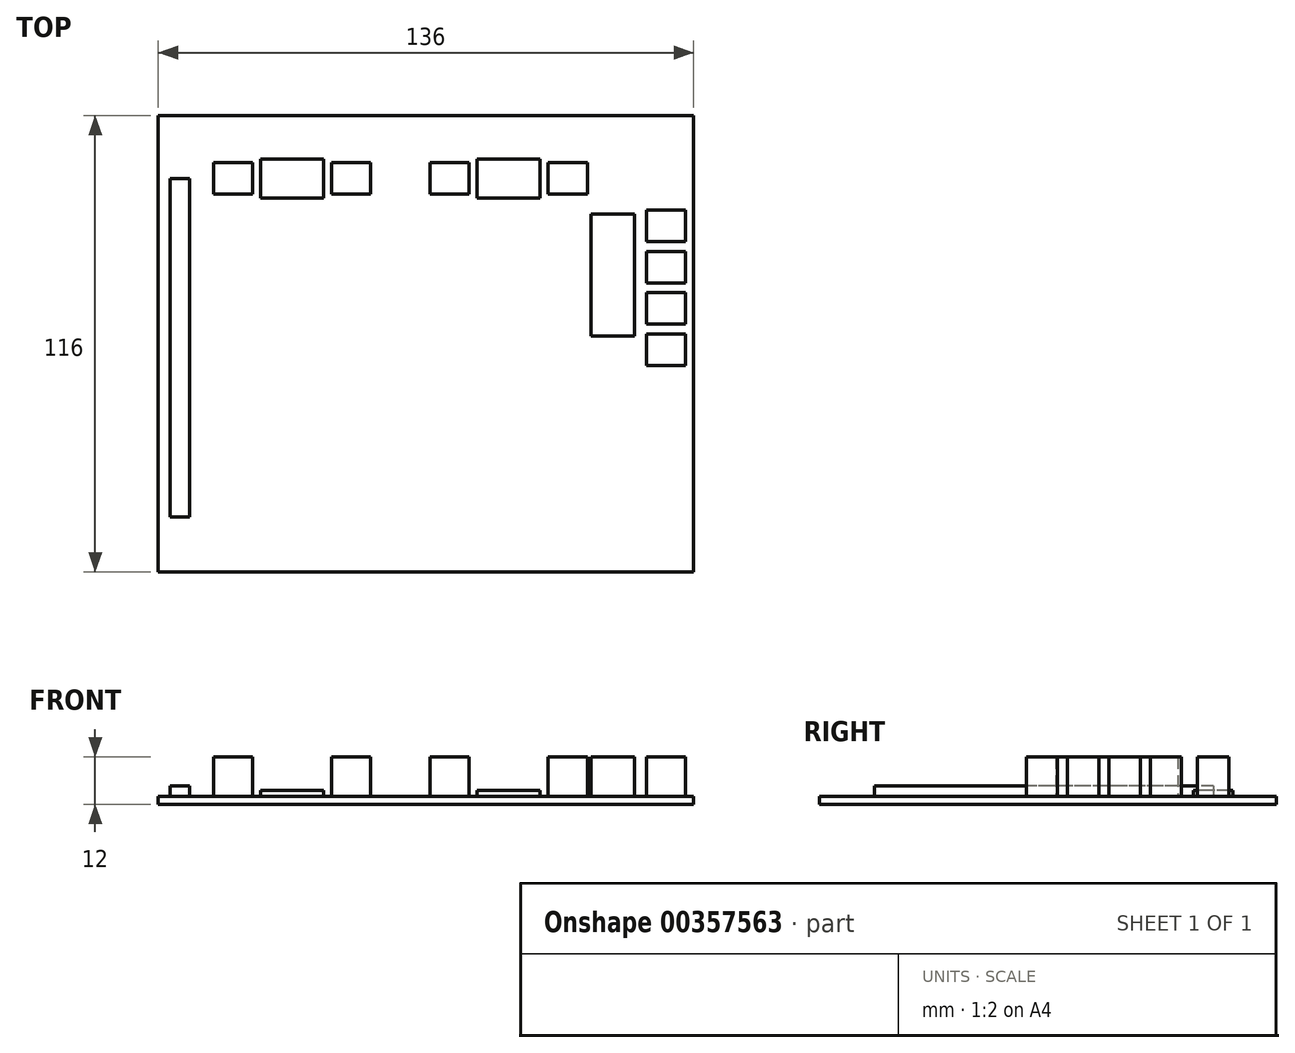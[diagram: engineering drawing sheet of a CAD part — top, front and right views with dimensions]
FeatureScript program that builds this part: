
annotation { "Feature Type Name" : "Feature", "Feature Type Description" : "" }
export const myFeature = defineFeature(function(context is Context, id is Id, definition is map)
    precondition{}
    {
        {
            var Q0;
            Q0=qCreatedBy(makeId("Top.planeOp"),FACE);
            var sketch = newSketch(context, id + "F0", { "sketchPlane" : qUnion([Q0])});
            skLineSegment(sketch, "E0.bottom", {"start": v(-68, -58) * mm, "end": v(68, -58) * mm});
            skLineSegment(sketch, "E0.top", {"start": v(-68, 58) * mm, "end": v(68, 58) * mm});
            skLineSegment(sketch, "E0.left", {"start": v(-68, -58) * mm, "end": v(-68, 58) * mm});
            skLineSegment(sketch, "E0.right", {"start": v(68, -58) * mm, "end": v(68, 58) * mm});
            skPoint(sketch, "E0.middle", {"position": v(0, 0) * mm});
            skSolve(sketch);
        }
        {
            var Q0;
            Q0=makeQuery(id+"F0.imprint","IMPRINT",FACE,{"disambiguationData":[TD([[makeQuery(id+"F0.imprint","IMPRINT",EDGE,{"derivedFrom":sQuery(id+"F0.wireOp",EDGE,"E0.bottom")}),1.0]])]});
            extrude(context, id + "F1", {"entities" : qUnion([Q0]), "endBound" : BoundingType.SYMMETRIC, "depth" : 2 * mm});
        }
        {
            var Q0;
            Q0=makeQuery(id+"F1.opExtrude","CAP_FACE",FACE,{"disambiguationData":[OSD([sQuery(id+"F0.wireOp",EDGE,"E0.bottom"),sQuery(id+"F0.wireOp",EDGE,"E0.top"),sQuery(id+"F0.wireOp",EDGE,"E0.left"),sQuery(id+"F0.wireOp",EDGE,"E0.right")])],"isStart":false});
            var sketch = newSketch(context, id + "F2", { "sketchPlane" : qUnion([Q0])});
            skLineSegment(sketch, "E1.bottom", {"start": v(53, 2) * mm, "end": v(42, 2) * mm});
            skLineSegment(sketch, "E1.top", {"start": v(53, 33) * mm, "end": v(42, 33) * mm});
            skLineSegment(sketch, "E1.left", {"start": v(53, 2) * mm, "end": v(53, 33) * mm});
            skLineSegment(sketch, "E1.right", {"start": v(42, 2) * mm, "end": v(42, 33) * mm});
            skPoint(sketch, "E1.middle", {"position": v(47.5, 17.5) * mm});
            skLineSegment(sketch, "E2.bottom", {"start": v(29, 37) * mm, "end": v(13, 37) * mm});
            skLineSegment(sketch, "E2.top", {"start": v(29, 47) * mm, "end": v(13, 47) * mm});
            skLineSegment(sketch, "E2.left", {"start": v(29, 47) * mm, "end": v(29, 37) * mm});
            skLineSegment(sketch, "E2.right", {"start": v(13, 47) * mm, "end": v(13, 37) * mm});
            skLineSegment(sketch, "E3.bottom", {"start": v(-26, 37) * mm, "end": v(-42, 37) * mm});
            skLineSegment(sketch, "E3.top", {"start": v(-26, 47) * mm, "end": v(-42, 47) * mm});
            skLineSegment(sketch, "E3.left", {"start": v(-26, 47) * mm, "end": v(-26, 37) * mm});
            skLineSegment(sketch, "E3.right", {"start": v(-42, 47) * mm, "end": v(-42, 37) * mm});
            skLineSegment(sketch, "E4.bottom", {"start": v(-65, 42) * mm, "end": v(-60, 42) * mm});
            skLineSegment(sketch, "E4.top", {"start": v(-65, -44) * mm, "end": v(-60, -44) * mm});
            skLineSegment(sketch, "E4.left", {"start": v(-65, 42) * mm, "end": v(-65, -44) * mm});
            skLineSegment(sketch, "E4.right", {"start": v(-60, 42) * mm, "end": v(-60, -44) * mm});
            skLineSegment(sketch, "E5.bottom", {"start": v(-54, 46) * mm, "end": v(-44, 46) * mm});
            skLineSegment(sketch, "E5.top", {"start": v(-54, 38) * mm, "end": v(-44, 38) * mm});
            skLineSegment(sketch, "E5.left", {"start": v(-54, 46) * mm, "end": v(-54, 38) * mm});
            skLineSegment(sketch, "E5.right", {"start": v(-44, 46) * mm, "end": v(-44, 38) * mm});
            skLineSegment(sketch, "E6.bottom", {"start": v(-24, 46) * mm, "end": v(-14, 46) * mm});
            skLineSegment(sketch, "E6.top", {"start": v(-24, 38) * mm, "end": v(-14, 38) * mm});
            skLineSegment(sketch, "E6.left", {"start": v(-24, 46) * mm, "end": v(-24, 38) * mm});
            skLineSegment(sketch, "E6.right", {"start": v(-14, 46) * mm, "end": v(-14, 38) * mm});
            skLineSegment(sketch, "E7.bottom", {"start": v(1, 46) * mm, "end": v(11, 46) * mm});
            skLineSegment(sketch, "E7.top", {"start": v(1, 38) * mm, "end": v(11, 38) * mm});
            skLineSegment(sketch, "E7.left", {"start": v(1, 46) * mm, "end": v(1, 38) * mm});
            skLineSegment(sketch, "E7.right", {"start": v(11, 46) * mm, "end": v(11, 38) * mm});
            skLineSegment(sketch, "E8.bottom", {"start": v(31, 46) * mm, "end": v(41, 46) * mm});
            skLineSegment(sketch, "E8.top", {"start": v(31, 38) * mm, "end": v(41, 38) * mm});
            skLineSegment(sketch, "E8.left", {"start": v(31, 46) * mm, "end": v(31, 38) * mm});
            skLineSegment(sketch, "E8.right", {"start": v(41, 46) * mm, "end": v(41, 38) * mm});
            skLineSegment(sketch, "E9.bottom", {"start": v(56, 34) * mm, "end": v(66, 34) * mm});
            skLineSegment(sketch, "E9.top", {"start": v(56, 26) * mm, "end": v(66, 26) * mm});
            skLineSegment(sketch, "E9.left", {"start": v(56, 34) * mm, "end": v(56, 26) * mm});
            skLineSegment(sketch, "E9.right", {"start": v(66, 34) * mm, "end": v(66, 26) * mm});
            skLineSegment(sketch, "E10.bottom", {"start": v(56, 23.5) * mm, "end": v(66, 23.5) * mm});
            skLineSegment(sketch, "E10.top", {"start": v(56, 15.5) * mm, "end": v(66, 15.5) * mm});
            skLineSegment(sketch, "E10.left", {"start": v(56, 23.5) * mm, "end": v(56, 15.5) * mm});
            skLineSegment(sketch, "E10.right", {"start": v(66, 23.5) * mm, "end": v(66, 15.5) * mm});
            skLineSegment(sketch, "E11.bottom", {"start": v(56, 13) * mm, "end": v(66, 13) * mm});
            skLineSegment(sketch, "E11.top", {"start": v(56, 5) * mm, "end": v(66, 5) * mm});
            skLineSegment(sketch, "E11.left", {"start": v(56, 13) * mm, "end": v(56, 5) * mm});
            skLineSegment(sketch, "E11.right", {"start": v(66, 13) * mm, "end": v(66, 5) * mm});
            skLineSegment(sketch, "E12.bottom", {"start": v(56, 2.5) * mm, "end": v(66, 2.5) * mm});
            skLineSegment(sketch, "E12.top", {"start": v(56, -5.5) * mm, "end": v(66, -5.5) * mm});
            skLineSegment(sketch, "E12.left", {"start": v(56, 2.5) * mm, "end": v(56, -5.5) * mm});
            skLineSegment(sketch, "E12.right", {"start": v(66, 2.5) * mm, "end": v(66, -5.5) * mm});
            skSolve(sketch);
        }
        {
            var Q0;
            Q0 = qSketchRegion(id + "F2", true);
            extrude(context, id + "F3", {"entities" : qUnion([Q0]), "operationType" : NewBodyOperationType.ADD, "depth" : 10 * mm});
        }
        {
            var Q0;
            Q0=makeQuery(id+"F3.opExtrude","CAP_FACE",FACE,{"disambiguationData":[OSD([sQuery(id+"F2.wireOp",EDGE,"E4.bottom"),sQuery(id+"F2.wireOp",EDGE,"E4.top"),sQuery(id+"F2.wireOp",EDGE,"E4.left"),sQuery(id+"F2.wireOp",EDGE,"E4.right")])],"isStart":false});
            extrude(context, id + "F4", {"entities" : qUnion([Q0]), "operationType" : NewBodyOperationType.REMOVE, "oppositeDirection" : true, "depth" : 7.3 * mm});
        }
        {
            var Q0;
            Q0=makeQuery(id+"F3.opExtrude","CAP_FACE",FACE,{"disambiguationData":[OSD([sQuery(id+"F2.wireOp",EDGE,"E3.bottom"),sQuery(id+"F2.wireOp",EDGE,"E3.top"),sQuery(id+"F2.wireOp",EDGE,"E3.left"),sQuery(id+"F2.wireOp",EDGE,"E3.right")])],"isStart":false});
            var Q1;
            Q1=makeQuery(id+"F3.opExtrude","CAP_FACE",FACE,{"disambiguationData":[OSD([sQuery(id+"F2.wireOp",EDGE,"E2.bottom"),sQuery(id+"F2.wireOp",EDGE,"E2.top"),sQuery(id+"F2.wireOp",EDGE,"E2.left"),sQuery(id+"F2.wireOp",EDGE,"E2.right")])],"isStart":false});
            extrude(context, id + "F5", {"entities" : qUnion([Q0, Q1]), "operationType" : NewBodyOperationType.REMOVE, "oppositeDirection" : true, "depth" : 8.5 * mm});
        }
    });
